# Revit family: Faucet-Two_Handle-American_Standard-Monterrey-5500174.002
name_source: partatom
category: Plumbing Fixtures
units: mm (PartAtom-declared; Revit-internal decimal feet)

## family parameters
Always vertical = No
Cut with Voids When Loaded = No
OmniClass Number = 23.45.55.17
OmniClass Title = Mixing Faucets
Part Type = Normal
Room Calculation Point = No
Round Connector Dimension = Use Diameter
Shared = Yes
Work Plane-Based = Yes

## types (1)
- 5500174.002
    ADA Compliant = Yes
    Assembly Code = D2020300
    CEC Compliant = Yes
    CW Connection = Yes
    CWFU = 1.5
    CalGreen Compliant = Yes
    Cold Water Connection Diameter = 1/2"
    Compliance Certifications = These products meet or exceed the following codes and standards: ANSI A117.1, ASME A112.18.1, CSA B 125, NSF 372. CALGreen
    Default Elevation = 0"
    Description = Monterrey® 4-Inch Centerset Cast Faucet With Wrist Blade Handles 0.35 gpm/1.3 Lpm
    Finish = Brass-American Standard-002-Polished Chrome
    Flow Rate = 5500174.002
    HW Connection = Yes
    HWFU = 1.5
    Height = 2 3/4"
    Hot Water Connection Diameter = 1/2"
    Installation Type = Deck Mounted
    Length = 3 3/4"
    Manufacturer = American Standard
    Material = Brass-American Standard-002-Polished Chrome
    Model = 0.35 gpm (1.3 Lpm)
    Product Documentation Link = https://americanstandard.box.com
    Product Page URL = https://www.americanstandard-us.com
    Revised Date = 09/20/2022
    URL = http://www.americanstandard-us.com
    Vent Connection = No
    WFU = 2
    Waste Connection = No
    Width = 11 3/4"

## geometry (parser evidence)
native form markers: Sweep x2
no freeform markers — native parametric forms only
